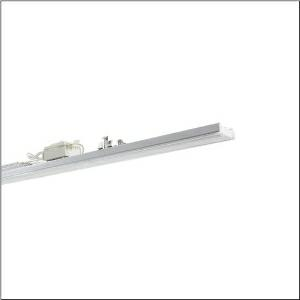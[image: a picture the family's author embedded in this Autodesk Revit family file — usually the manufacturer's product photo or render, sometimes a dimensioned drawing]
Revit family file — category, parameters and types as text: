
# Revit family: licross_21_recessed_ho_52te12dn4fxm
name_source: partatom
category: Lighting Fixtures
units: mm (PartAtom-declared; Revit-internal decimal feet)

## family parameters
Cut with Voids When Loaded = No
Host = Face
Light Source = No
Part Type = Normal
Room Calculation Point = No
Round Connector Dimension = Use Diameter
Shared = No

## types (1)
- --- (1 x LED, 15000 lm, 84.6 W, 4000K)
    Apparent Load = 85 VA
    CIE Flux Codes = 69 91 98 100 100
    Color Rendering = 80
    Color Temperature = 4000K
    Default Elevation = 1800 mm
    Description = Licross 21 Recessed HO, luminaire insert, of sheet steel, galvanised, coil coated, white, length: 1.500mm, width: 66mm, height: 67mm, LED rated luminous flux: 15.000lm, light colour: 840, SDCM (Standard Deviation of Colour Matching)MacAdam ≤ 3 SDCM (initial), control gear: DALI 2, with plug, 5-pole, with phase selection, mains connection: 220..240V, AC, 50/60Hz, rated input power: 85W, internal wiring halogen-free, primary optical cover: cover, of PMMA, light emission: direct distribution, primary light characteristic: symmetric, protection rating (complete): IP54, insulation class (complete): insulation class I (protective earthing), certification: CE, ENEC, VDE, UKCA, protection symbol: D if used in an environment with non-conductive dust loads with corresponding accessories, impact resistance: IK06, permissible ambient temperature for indoor applications: -25..+30°C, corresponds to IFS (International Featured Standards) requirements for safety and quality in the food industry, reducing of maximum allowable ambient temperature of 5°C with ceiling mounting, LABS conformity tested according to VDMA 24364:2018-05, The light source and the operating device comply with the requirements of the Ecodesign Regulation (EU) 2019/2020 and are replaceable in accordance with this regulation, packaging unit: 1 piece
    Height = 58 mm
    Lamp = 1 x LED
    Lamp Light Flux = 15000 lm
    Lamp Power = 84.6 W
    Lamp count = 1
    Length = 1500 mm
    Luminous efficacy = 177 lm/W
    Manufacturer = Siteco
    ModVariant = No
    Model = 52TE12DN4FXM
    Mounting Place = Ceiling
    Mounting Type = Pendant
    Number of Poles = 1
    OnlyDefault = Yes
    Power Factor = 1
    Product Name = Licross 21 Recessed HO
    Product group = luminaire insert | ceiling pendant
    ProductGroupID = 901
    Protection Class = Protection class I
    Protection Degree = IP 54
    RLX_Detail_Level = 1
    RLX_Emergency_Light_Flux = 0 lm
    RLX_Emergency_Type = 0
    RLX_Emergency_Type_DB = No
    RlxData = <blob elided: 24957 chars, md5=109339fa>
    Socket = socket
    Standby Power = 0 W
    System Light Flux = 15000 lm
    System Power = 85 W
    Type Comments = factory setting: luminous flux: 100 % | dim-lin: 254 | 484 mA
    Type Image = l_1296930.jpg
    URL = http://relux.com
    VarID = @adj_116601
    Voltage = 0 V
    Weight = 0.00 kg
    Width = 66 mm

## geometry (parser evidence)
native form markers: Blend x4, Sweep x11
no freeform markers — native parametric forms only
